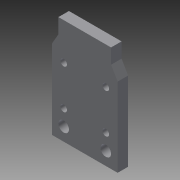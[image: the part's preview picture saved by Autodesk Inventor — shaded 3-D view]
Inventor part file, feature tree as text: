
AUTODESK INVENTOR PART (.ipt)
format: ipt  version: 2013 (Build 170138000, 138)  size: 121,344 bytes
history: native  units: mm
features: sketch x4, extrude x2, hole x2, other x1
ambient origin geometry x8: Origin, YZ Plane, XZ Plane, XY Plane, X Axis, Y Axis, Z Axis, Center Point
feature tree (9):
  other  "ソリッド1"
  extrude  "押し出し1"  Depth=25.0mm
  extrude  "押し出し2"  Depth=40.0mm
  hole  "穴1"  [1 undecoded]
  hole  "穴2"  [1 undecoded]
  sketch  "スケッチ1"
  sketch  "スケッチ2"
  sketch  "スケッチ3"
  sketch  "スケッチ4"
note: 2 required parameter values undecoded (feature->parameter linkage not recoverable at this tier; creation-order binding heuristic only, values carry confidence <= 0.55)
